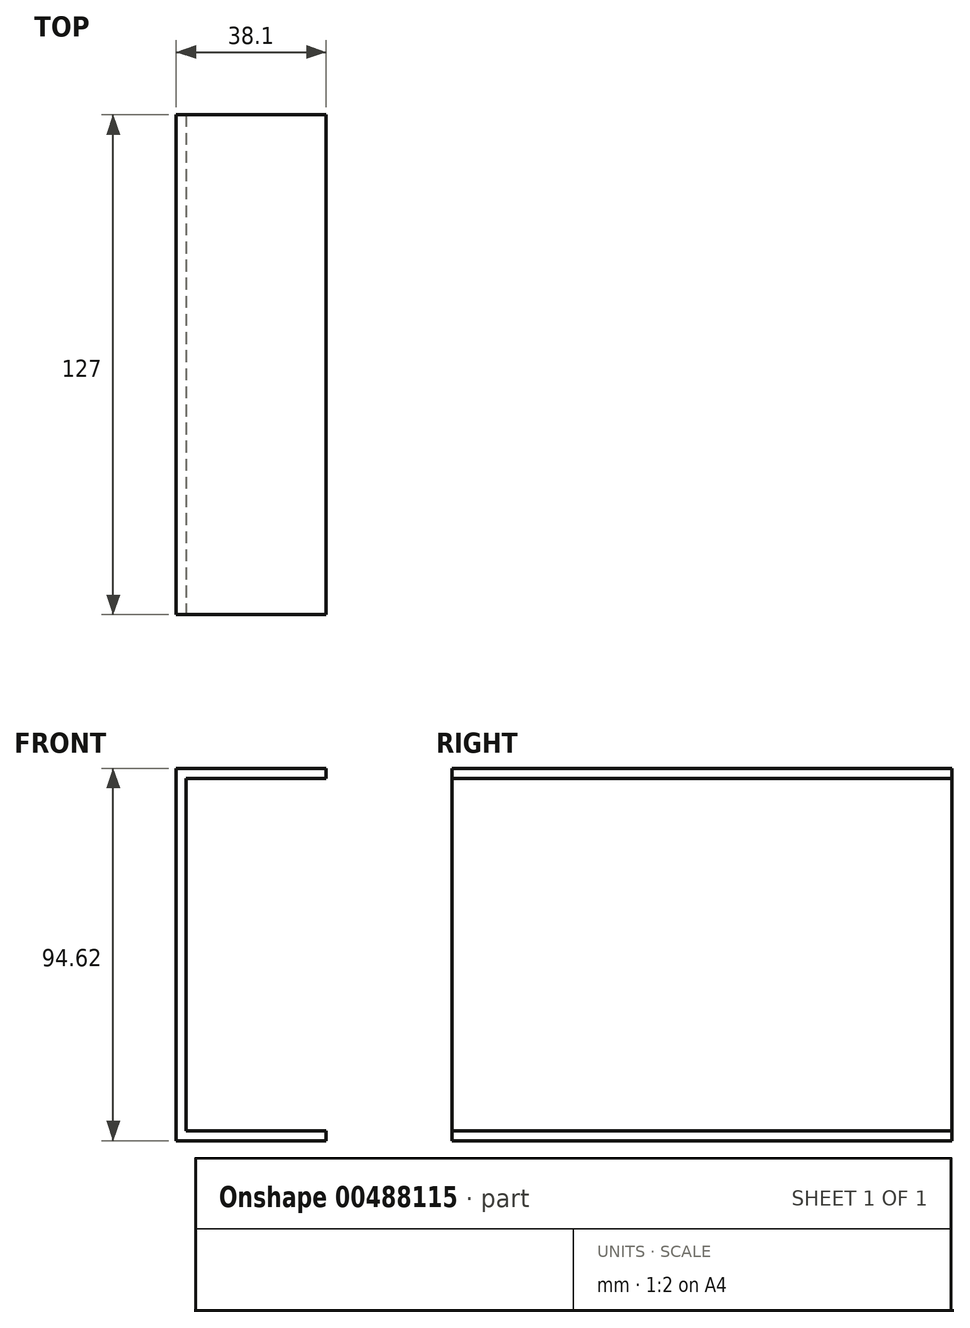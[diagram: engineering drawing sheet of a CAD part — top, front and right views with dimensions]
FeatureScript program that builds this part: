
annotation { "Feature Type Name" : "Feature", "Feature Type Description" : "" }
export const myFeature = defineFeature(function(context is Context, id is Id, definition is map)
    precondition{}
    {
        {
            var Q0;
            Q0=qCreatedBy(makeId("Right.planeOp"),FACE);
            var sketch = newSketch(context, id + "F0", { "sketchPlane" : qUnion([Q0])});
            skLineSegment(sketch, "E0.bottom", {"start": v(63.5, 47.3) * mm, "end": v(-63.5, 47.3) * mm});
            skLineSegment(sketch, "E0.top", {"start": v(63.5, -47.3) * mm, "end": v(-63.5, -47.3) * mm});
            skLineSegment(sketch, "E0.left", {"start": v(63.5, 47.3) * mm, "end": v(63.5, -47.3) * mm});
            skLineSegment(sketch, "E0.right", {"start": v(-63.5, 47.3) * mm, "end": v(-63.5, -47.3) * mm});
            skPoint(sketch, "E0.middle", {"position": v(0, 0) * mm});
            skSolve(sketch);
        }
        {
            var Q0;
            Q0=makeQuery(id+"F0.imprint","IMPRINT",FACE,{"disambiguationData":[TD([[makeQuery(id+"F0.imprint","IMPRINT",EDGE,{"derivedFrom":sQuery(id+"F0.wireOp",EDGE,"E0.bottom")}),1.0]])]});
            extrude(context, id + "F1", {"entities" : qUnion([Q0]), "depth" : 38.1 * mm});
        }
        {
            var Q0;
            Q0=makeQuery(id+"F1.opExtrude","CAP_FACE",FACE,{"disambiguationData":[OSD([sQuery(id+"F0.wireOp",EDGE,"E0.bottom"),sQuery(id+"F0.wireOp",EDGE,"E0.top"),sQuery(id+"F0.wireOp",EDGE,"E0.left"),sQuery(id+"F0.wireOp",EDGE,"E0.right")])],"isStart":false});
            var Q1;
            Q1=makeQuery(id+"F1.opExtrude","SWEPT_FACE",FACE,{"disambiguationData":[OSD([sQuery(id+"F0.wireOp",EDGE,"E0.right")])]});
            var Q2;
            Q2=makeQuery(id+"F1.opExtrude","SWEPT_FACE",FACE,{"disambiguationData":[OSD([sQuery(id+"F0.wireOp",EDGE,"E0.left")])]});
            shell(context, id + "F2", {"entities" : qUnion([Q0, Q1, Q2]), "thickness" : 2.54 * mm});
        }
    });
